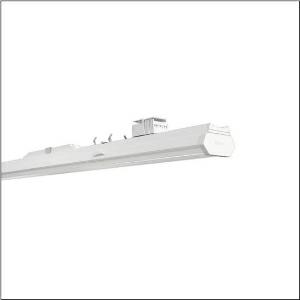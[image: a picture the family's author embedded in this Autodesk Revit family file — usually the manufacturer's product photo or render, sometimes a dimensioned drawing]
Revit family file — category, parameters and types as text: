
# Revit family: licross_r__21_protected_mo_52td12dn4a5g_44fa
name_source: partatom
category: Lighting Fixtures
units: mm (PartAtom-declared; Revit-internal decimal feet)

## family parameters
Cut with Voids When Loaded = No
Host = Face
Light Source = No
Part Type = Normal
Room Calculation Point = No
Round Connector Dimension = Use Diameter
Shared = No

## types (1)
- --- (1 x LED, 10700 lm, 62 W, 4000K)
    Apparent Load = 62 VA
    CIE Flux Codes = 73 92 98 99 100
    Color Rendering = 80
    Color Temperature = 4000K
    Default Elevation = 1800 mm
    Description = Licross® 21 Protected MO, luminaire insert, of sheet steel, galvanised, coil coated, white, length: 1.500mm, width: 90mm, height: 103mm, LED rated luminous flux: 10.700lm, light colour: 840, control gear: DALI 2, with plug, 5-pole, with phase selection, mains connection: 220..240V, AC, 50/60Hz, rated input power: 62W, halogen-free wiring, primary light control with lens, of plastic, primary optical cover: cover, of PMMA, light emission: direct distribution, primary light characteristic: symmetric, protection rating (complete): IP54, insulation class (complete): insulation class I (protective earthing), certification: CE, ENEC, VDE, UKCA, protection symbol: D if used in an environment with non-conductive dust loads with corresponding accessories, impact resistance: IK06, permissible ambient temperature for indoor applications: -25..+35°C, corresponds to IFS (International Featured Standards) requirements for safety and quality in the food industry, reducing of maximum allowable ambient temperature of 5°C with ceiling mounting, LABS conformity tested according to VDMA 24364:2018-05, packaging unit: 1 piece
    Height = 92 mm
    Lamp = 1 x LED
    Lamp Light Flux = 10700 lm
    Lamp Power = 62 W
    Lamp count = 1
    Length = 1500 mm
    Luminous efficacy = 173 lm/W
    Manufacturer = Siteco
    ModVariant = No
    Model = 52TD12DN4A5G
    Mounting Place = Ceiling
    Mounting Type = Pendant
    Number of Poles = 1
    OnlyDefault = Yes
    Power Factor = 1
    Product Name = Licross® 21 Protected MO
    Product group = luminaire insert
    ProductGroupID = 902
    Protection Class = Protection class I
    Protection Degree = IP 54
    RLX_Detail_Level = 1
    RLX_Emergency_Light_Flux = 0 lm
    RLX_Emergency_Type = 0
    RLX_Emergency_Type_DB = No
    RlxData = <blob elided: 24469 chars, md5=7c72deb5>
    Socket = socket
    Standby Power = 0 W
    System Light Flux = 10700 lm
    System Power = 62 W
    Type Comments = factory setting: luminous flux: 100 % | dim-lin: 254 | 418 mA
    Type Image = l_1256148.jpg
    URL = http://relux.com
    VarID = @adj_128762
    Voltage = 0 V
    Weight = 0.00 kg
    Width = 88 mm

## geometry (parser evidence)
native form markers: Blend x4, Sweep x11
no freeform markers — native parametric forms only
